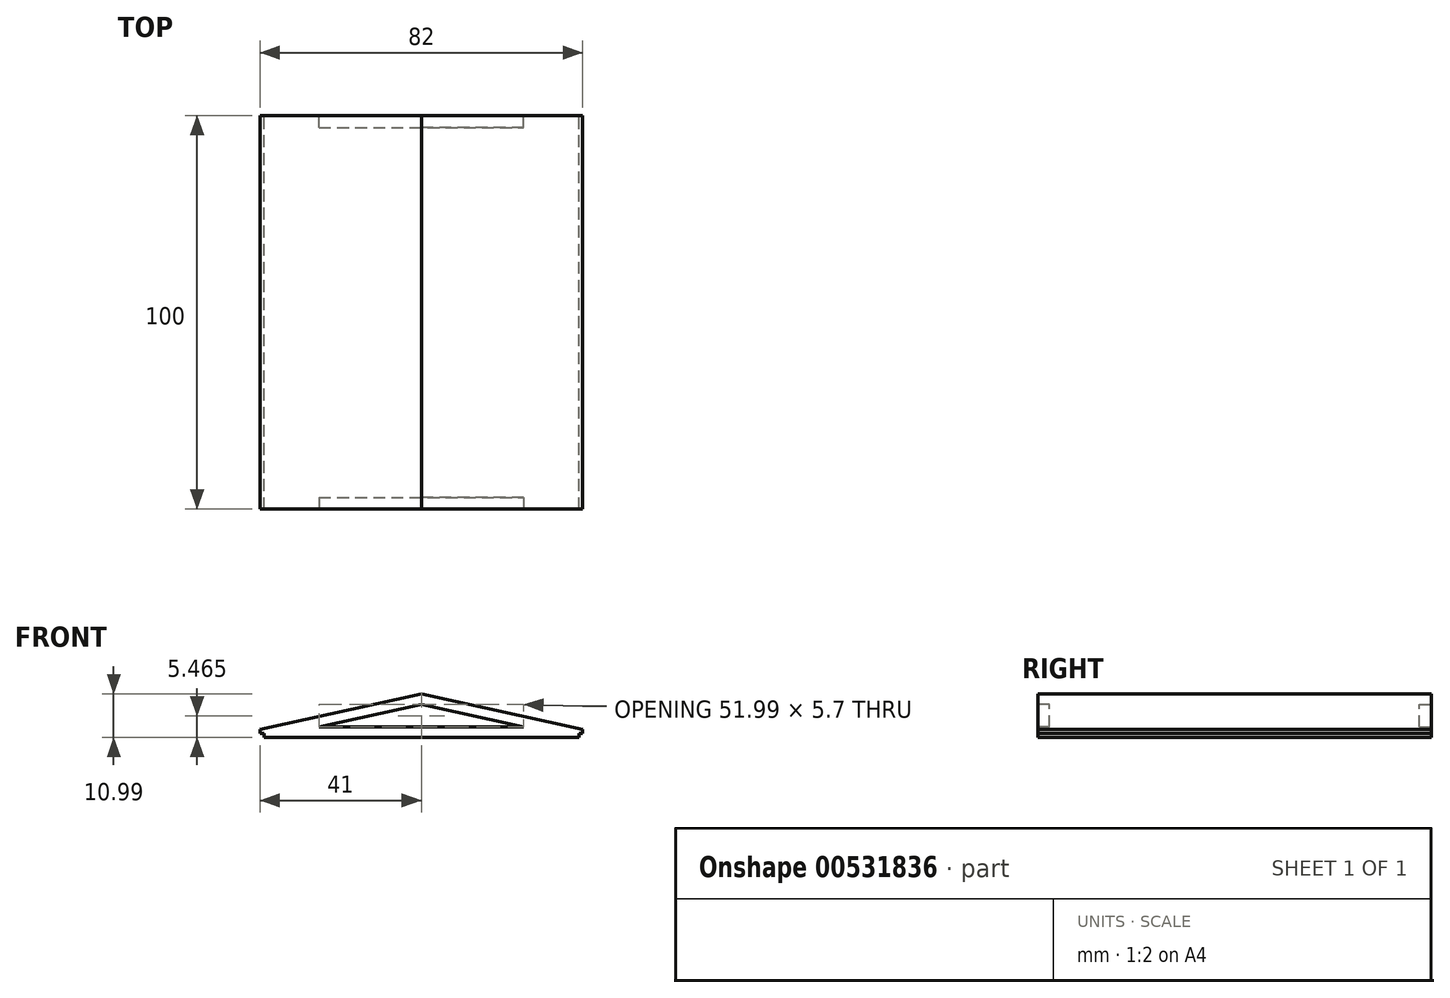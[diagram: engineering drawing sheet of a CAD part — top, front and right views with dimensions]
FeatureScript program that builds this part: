
annotation { "Feature Type Name" : "Feature", "Feature Type Description" : "" }
export const myFeature = defineFeature(function(context is Context, id is Id, definition is map)
    precondition{}
    {
        {
            var Q0;
            Q0=qCreatedBy(makeId("Front.planeOp"),FACE);
            var sketch = newSketch(context, id + "F0", { "sketchPlane" : qUnion([Q0])});
            skLineSegment(sketch, "E0", {"start": v(0, 0) * mm, "end": v(40, 0) * mm});
            skLineSegment(sketch, "E1", {"start": v(40, 0) * mm, "end": v(40, 1) * mm});
            skLineSegment(sketch, "E2", {"start": v(40, 1) * mm, "end": v(41, 1) * mm});
            skLineSegment(sketch, "E3", {"start": v(41, 1) * mm, "end": v(41, 2) * mm});
            skPoint(sketch, "E4.end.orphan", {"position": v(0, 11) * mm});
            skLineSegment(sketch, "E5", {"start": v(41, 2) * mm, "end": v(0, 11) * mm});
            skLineSegment(sketch, "E6.MirrorCS", {"start": v(-40, 0) * mm, "end": v(-40, 1) * mm});
            skLineSegment(sketch, "E7.MirrorCS", {"start": v(-40, 1) * mm, "end": v(-41, 1) * mm});
            skLineSegment(sketch, "E8.MirrorCS", {"start": v(-41, 1) * mm, "end": v(-41, 2) * mm});
            skLineSegment(sketch, "E9.MirrorCS", {"start": v(-41, 2) * mm, "end": v(0, 11) * mm});
            skLineSegment(sketch, "E10.MirrorCS", {"start": v(0, 0) * mm, "end": v(-40, 0) * mm});
            skSolve(sketch);
        }
        {
            var Q0;
            Q0 = qSketchRegion(id + "F0", true);
            extrude(context, id + "F1", {"entities" : qUnion([Q0]), "depth" : 100 * mm, "offsetDistance" : 25 * mm});
        }
        {
            var Q0;
            Q0=makeQuery(id+"F1.opExtrude","CAP_FACE",FACE,{"disambiguationData":[OSD([sQuery(id+"F0.wireOp",EDGE,"E0"),sQuery(id+"F0.wireOp",EDGE,"E1"),sQuery(id+"F0.wireOp",EDGE,"E2"),sQuery(id+"F0.wireOp",EDGE,"E3"),sQuery(id+"F0.wireOp",EDGE,"E5"),sQuery(id+"F0.wireOp",EDGE,"E6.MirrorCS"),sQuery(id+"F0.wireOp",EDGE,"E7.MirrorCS"),sQuery(id+"F0.wireOp",EDGE,"E8.MirrorCS"),sQuery(id+"F0.wireOp",EDGE,"E9.MirrorCS"),sQuery(id+"F0.wireOp",EDGE,"E10.MirrorCS")])],"isStart":true});
            var sketch = newSketch(context, id + "F2", { "sketchPlane" : qUnion([Q0])});
            skLineSegment(sketch, "E11.0", {"start": v(-41, 2) * mm, "end": v(0, 11) * mm});
            skLineSegment(sketch, "E12", {"start": v(-26, 2.61) * mm, "end": v(0, 8.32) * mm});
            skLineSegment(sketch, "E13", {"start": v(0, 8.32) * mm, "end": v(0, 2.61) * mm});
            skLineSegment(sketch, "E14", {"start": v(0, 2.61) * mm, "end": v(-26, 2.61) * mm});
            skLineSegment(sketch, "E15.MirrorCS", {"start": v(26, 2.61) * mm, "end": v(0, 8.32) * mm});
            skLineSegment(sketch, "E16.MirrorCS", {"start": v(0, 2.61) * mm, "end": v(26, 2.61) * mm});
            skSolve(sketch);
        }
        {
            var Q0;
            Q0 = qSketchRegion(id + "F2", true);
            extrude(context, id + "F3", {"entities" : qUnion([Q0]), "operationType" : NewBodyOperationType.REMOVE, "oppositeDirection" : true, "depth" : 3 * mm, "offsetDistance" : 25 * mm});
        }
        {
            var Q0;
            Q0=makeQuery(id+"F1.opExtrude","CAP_FACE",FACE,{"disambiguationData":[OSD([sQuery(id+"F0.wireOp",EDGE,"E0"),sQuery(id+"F0.wireOp",EDGE,"E1"),sQuery(id+"F0.wireOp",EDGE,"E2"),sQuery(id+"F0.wireOp",EDGE,"E3"),sQuery(id+"F0.wireOp",EDGE,"E5"),sQuery(id+"F0.wireOp",EDGE,"E6.MirrorCS"),sQuery(id+"F0.wireOp",EDGE,"E7.MirrorCS"),sQuery(id+"F0.wireOp",EDGE,"E8.MirrorCS"),sQuery(id+"F0.wireOp",EDGE,"E9.MirrorCS"),sQuery(id+"F0.wireOp",EDGE,"E10.MirrorCS")])],"isStart":false});
            var sketch = newSketch(context, id + "F4", { "sketchPlane" : qUnion([Q0])});
            skLineSegment(sketch, "E17.0", {"start": v(26, 2.61) * mm, "end": v(0, 8.32) * mm});
            skLineSegment(sketch, "E18.0", {"start": v(0, 2.61) * mm, "end": v(26, 2.61) * mm});
            skLineSegment(sketch, "E19.0", {"start": v(-26, 2.61) * mm, "end": v(0, 8.32) * mm});
            skLineSegment(sketch, "E20.0", {"start": v(0, 2.61) * mm, "end": v(-26, 2.61) * mm});
            skSolve(sketch);
        }
        {
            var Q0;
            Q0 = qSketchRegion(id + "F4", true);
            extrude(context, id + "F5", {"entities" : qUnion([Q0]), "operationType" : NewBodyOperationType.REMOVE, "oppositeDirection" : true, "depth" : 3 * mm, "offsetDistance" : 25 * mm});
        }
    });
